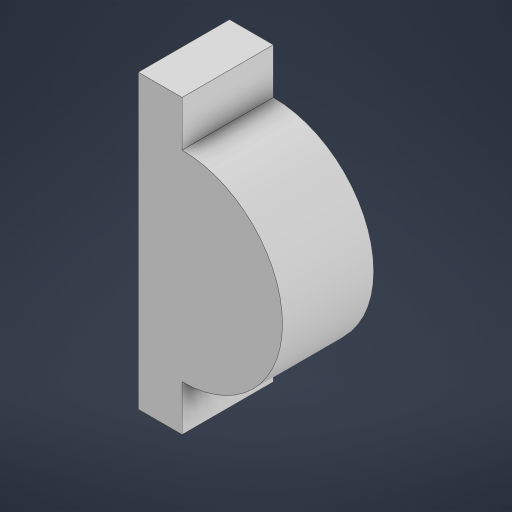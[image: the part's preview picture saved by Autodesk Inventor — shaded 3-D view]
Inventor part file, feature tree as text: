
AUTODESK INVENTOR PART (.ipt)
format: ipt  version: 2023 (Build 270158000, 158)  size: 176,128 bytes
history: native  units: in
note: dims shown in document units (in); Inventor stores cm internally (conversion verified against a paired STEP export)
features: extrude x1, sketch x1
ambient origin geometry x8: Origin, YZ Plane, XZ Plane, XY Plane, X Axis, Y Axis, Z Axis, Center Point
bodies: Solid1 (feature_tree)
feature tree (2):
  extrude  "Extrusion1"  Depth=0.126in
  sketch  "Sketch1"  dims[d0=0.0189in d1=0.126in d5=0.0394in d6=0.0in d7=0.0866in]
